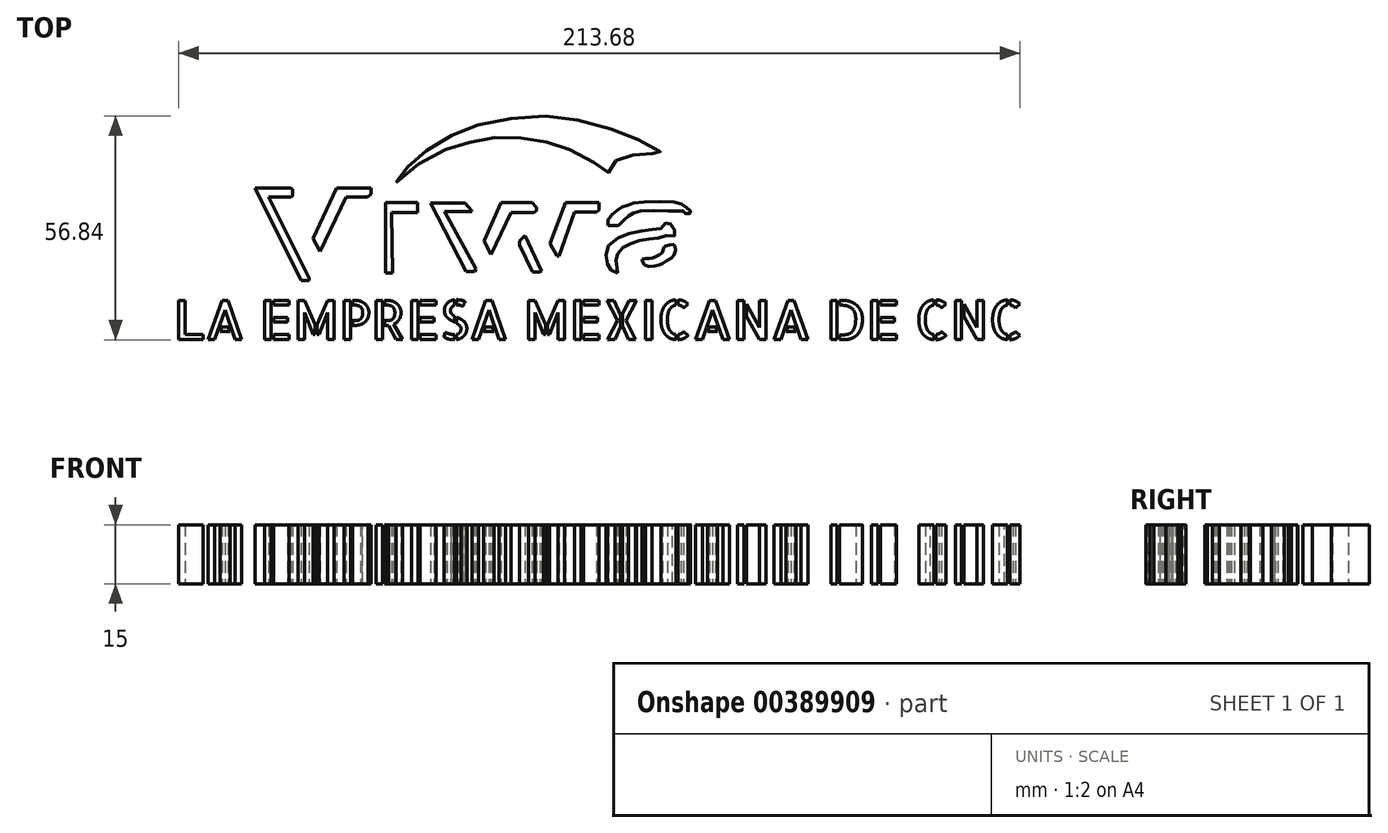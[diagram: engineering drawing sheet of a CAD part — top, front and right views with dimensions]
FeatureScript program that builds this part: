
annotation { "Feature Type Name" : "Feature", "Feature Type Description" : "" }
export const myFeature = defineFeature(function(context is Context, id is Id, definition is map)
    precondition{}
    {
        {
            var Q0;
            Q0=qCreatedBy(makeId("Top.planeOp"),FACE);
            var sketch = newSketch(context, id + "F0", { "sketchPlane" : qUnion([Q0])});
            skLineSegment(sketch, "E0", {"start": v(-40.3, 7.2) * mm, "end": v(-42.29, 7.2) * mm});
            skLineSegment(sketch, "E1", {"start": v(-42.29, 7.2) * mm, "end": v(-54.09, 30.73) * mm});
            skLineSegment(sketch, "E2", {"start": v(-54.09, 30.73) * mm, "end": v(-45.17, 30.73) * mm});
            skLineSegment(sketch, "E3", {"start": v(-45.17, 30.73) * mm, "end": v(-44.48, 30.45) * mm});
            skLineSegment(sketch, "E4", {"start": v(-44.48, 30.45) * mm, "end": v(-44.48, 28.7) * mm});
            skLineSegment(sketch, "E5", {"start": v(-44.48, 28.7) * mm, "end": v(-44.86, 28.36) * mm});
            skLineSegment(sketch, "E6", {"start": v(-44.86, 28.36) * mm, "end": v(-50.58, 28.36) * mm});
            skLineSegment(sketch, "E7", {"start": v(-50.58, 28.36) * mm, "end": v(-40.3, 7.78) * mm});
            skLineSegment(sketch, "E8", {"start": v(-40.3, 7.78) * mm, "end": v(-40.3, 7.2) * mm});
            skLineSegment(sketch, "E9", {"start": v(-37.5, 14.6) * mm, "end": v(-39.26, 17.86) * mm});
            skLineSegment(sketch, "E10", {"start": v(-39.26, 17.86) * mm, "end": v(-33.32, 30.7) * mm});
            skLineSegment(sketch, "E11", {"start": v(-33.32, 30.7) * mm, "end": v(-24.6, 30.7) * mm});
            skLineSegment(sketch, "E12", {"start": v(-24.6, 30.7) * mm, "end": v(-24.6, 29.12) * mm});
            skLineSegment(sketch, "E13", {"start": v(-24.6, 29.12) * mm, "end": v(-25.41, 28.36) * mm});
            skLineSegment(sketch, "E14", {"start": v(-25.41, 28.36) * mm, "end": v(-30.98, 28.36) * mm});
            skLineSegment(sketch, "E15", {"start": v(-30.98, 28.36) * mm, "end": v(-37.5, 14.6) * mm});
            skLineSegment(sketch, "E16", {"start": v(-19.06, 9.07) * mm, "end": v(-20.9, 9.07) * mm});
            skLineSegment(sketch, "E17", {"start": v(-20.9, 9.07) * mm, "end": v(-20.9, 27.04) * mm});
            skLineSegment(sketch, "E18", {"start": v(-20.9, 27.04) * mm, "end": v(-12.74, 27.04) * mm});
            skLineSegment(sketch, "E19", {"start": v(-12.74, 27.04) * mm, "end": v(-12.74, 24.52) * mm});
            skLineSegment(sketch, "E20", {"start": v(-12.74, 24.52) * mm, "end": v(-19.32, 24.52) * mm});
            skLineSegment(sketch, "E21", {"start": v(-19.32, 24.52) * mm, "end": v(-19.06, 9.07) * mm});
            skLineSegment(sketch, "E22", {"start": v(1.67, 9.46) * mm, "end": v(-0.44, 9.46) * mm});
            skLineSegment(sketch, "E23", {"start": v(-0.44, 9.46) * mm, "end": v(-9.5, 26.94) * mm});
            skLineSegment(sketch, "E24", {"start": v(-9.5, 26.94) * mm, "end": v(-0.74, 26.94) * mm});
            skLineSegment(sketch, "E25", {"start": v(-0.74, 26.94) * mm, "end": v(0.92, 25.02) * mm});
            skLineSegment(sketch, "E26", {"start": v(0.92, 25.02) * mm, "end": v(1.08, 24.71) * mm});
            skLineSegment(sketch, "E27", {"start": v(1.08, 24.71) * mm, "end": v(-5.85, 24.71) * mm});
            skLineSegment(sketch, "E28", {"start": v(-5.85, 24.71) * mm, "end": v(2.11, 10.07) * mm});
            skLineSegment(sketch, "E29", {"start": v(2.11, 10.07) * mm, "end": v(1.67, 9.46) * mm});
            skLineSegment(sketch, "E30", {"start": v(4.1, 17.22) * mm, "end": v(8.49, 26.97) * mm});
            skLineSegment(sketch, "E31", {"start": v(8.49, 26.97) * mm, "end": v(16.36, 26.97) * mm});
            skLineSegment(sketch, "E32", {"start": v(16.36, 26.97) * mm, "end": v(17.43, 25.72) * mm});
            skLineSegment(sketch, "E33", {"start": v(17.43, 25.72) * mm, "end": v(17.43, 25) * mm});
            skLineSegment(sketch, "E34", {"start": v(17.43, 25) * mm, "end": v(16.87, 24.52) * mm});
            skLineSegment(sketch, "E35", {"start": v(16.87, 24.52) * mm, "end": v(10.99, 24.52) * mm});
            skLineSegment(sketch, "E36", {"start": v(10.99, 24.52) * mm, "end": v(5.9, 13.87) * mm});
            skLineSegment(sketch, "E37", {"start": v(5.9, 13.87) * mm, "end": v(4.1, 17.22) * mm});
            skLineSegment(sketch, "E38", {"start": v(14.57, 18.65) * mm, "end": v(18.77, 9.66) * mm});
            skLineSegment(sketch, "E39", {"start": v(18.77, 9.66) * mm, "end": v(18.35, 9.3) * mm});
            skLineSegment(sketch, "E40", {"start": v(18.35, 9.3) * mm, "end": v(16.44, 9.3) * mm});
            skLineSegment(sketch, "E41", {"start": v(16.44, 9.3) * mm, "end": v(13.14, 16.2) * mm});
            skLineSegment(sketch, "E42", {"start": v(13.14, 16.2) * mm, "end": v(13.14, 17.22) * mm});
            skLineSegment(sketch, "E43", {"start": v(13.14, 17.22) * mm, "end": v(14.57, 18.65) * mm});
            skLineSegment(sketch, "E44", {"start": v(22.7, 13.37) * mm, "end": v(20.91, 16.54) * mm});
            skLineSegment(sketch, "E45", {"start": v(20.91, 16.54) * mm, "end": v(24.77, 26.96) * mm});
            skLineSegment(sketch, "E46", {"start": v(24.77, 26.96) * mm, "end": v(33.3, 26.96) * mm});
            skLineSegment(sketch, "E47", {"start": v(33.3, 26.96) * mm, "end": v(33.3, 25.07) * mm});
            skLineSegment(sketch, "E48", {"start": v(33.3, 25.07) * mm, "end": v(32.69, 24.54) * mm});
            skLineSegment(sketch, "E49", {"start": v(32.69, 24.54) * mm, "end": v(27.16, 24.54) * mm});
            skLineSegment(sketch, "E50", {"start": v(27.16, 24.54) * mm, "end": v(23.23, 13.45) * mm});
            skLineSegment(sketch, "E51", {"start": v(23.23, 13.45) * mm, "end": v(22.7, 13.37) * mm});
            skLineSegment(sketch, "E52", {"start": v(38.33, 21.2) * mm, "end": v(35.67, 21.2) * mm});
            skFitSpline(sketch, "E53", {"points": [v(35.67, 21.2) * mm, v(35.67, 22.79) * mm, v(37.4, 24.54) * mm, v(38.78, 25.7) * mm, v(41.01, 26.48) * mm, v(42.69, 26.93) * mm, v(52.87, 27.12) * mm, v(54.86, 26.27) * mm, v(56.49, 25.05) * mm, v(56.62, 24.54) * mm, v(56.33, 24.17) * mm, v(55.4, 24.17) * mm, v(54.94, 24.54) * mm, v(54.52, 24.89) * mm, v(53.4, 24.86) * mm, v(44.07, 24.86) * mm, v(41.65, 24.14) * mm, v(40.27, 23.16) * mm, v(38.33, 21.2) * mm], "startDerivative": vector(-7.24, 33.02) * mm, "endDerivative": vector(-30.8, -33.26) * mm});
            skFitSpline(sketch, "E54", {"points": [v(38.01, 9.14) * mm, v(36.65, 9.58) * mm, v(36.21, 10.4) * mm, v(35.39, 11.5) * mm, v(35.1, 13.66) * mm, v(35.67, 15.9) * mm, v(38.33, 18.12) * mm, v(41.87, 19.38) * mm, v(45.5, 20.01) * mm, v(47.75, 20.3) * mm, v(49.52, 20.65) * mm, v(50.15, 21.69) * mm, v(50.7, 21.94) * mm, v(51.39, 21.63) * mm, v(52.37, 20.7) * mm, v(52.59, 19.22) * mm, v(52.56, 18.56) * mm, v(51.17, 18.69) * mm, v(49.62, 18.3) * mm, v(47.85, 17.93) * mm, v(45.38, 17.64) * mm, v(43.2, 17.33) * mm, v(41.3, 16.57) * mm, v(39.53, 15.62) * mm, v(38.33, 14.35) * mm, v(37.73, 13.06) * mm, v(37.63, 12.01) * mm, v(37.82, 10.75) * mm, v(38.33, 9.7) * mm, v(38.01, 9.14) * mm]});
            skFitSpline(sketch, "E55", {"points": [v(44.3, 12.65) * mm, v(45.63, 12.84) * mm, v(46.61, 12.84) * mm, v(47.75, 13.34) * mm, v(48.86, 13.85) * mm, v(49.55, 14.48) * mm, v(49.68, 15.11) * mm, v(49.84, 15.62) * mm, v(50.76, 16.13) * mm, v(52.18, 16.35) * mm, v(52.62, 15.97) * mm, v(52.59, 14) * mm, v(51.58, 12.87) * mm, v(49.3, 11.45) * mm, v(47.88, 10.94) * mm, v(45.29, 10.97) * mm, v(44.43, 11.95) * mm, v(44.3, 12.65) * mm]});
            skFitSpline(sketch, "E56", {"points": [v(-18.25, 32.08) * mm, v(-16.37, 34.86) * mm, v(-11.71, 39.22) * mm, v(-4.34, 43.96) * mm, v(3.86, 47.04) * mm, v(16.56, 48.92) * mm, v(27.92, 48.02) * mm, v(39.42, 44.56) * mm, v(46.34, 41.4) * mm, v(49.5, 39.37) * mm, v(47.55, 39.45) * mm, v(43.18, 39.37) * mm, v(39.72, 38.47) * mm, v(37.02, 37.27) * mm, v(35.67, 35.16) * mm, v(35.67, 34.4) * mm, v(30.7, 38.17) * mm, v(24.16, 41.1) * mm, v(18, 42.9) * mm, v(10.55, 43.58) * mm, v(3.4, 43.13) * mm, v(-3.44, 41.03) * mm, v(-10.13, 38.54) * mm, v(-18.25, 32.08) * mm]});
            skText(sketch, "E57", { "text": "LA EMPRESA MEXICANA DE CNC", "fontName": "AllertaStencil-Regular.ttf"});
            const initialGuessF0  = {"E57": [-0.0747, -0.00779, 1, 0, 0.00996]};
            skSetInitialGuess(sketch, initialGuessF0);
            skSolve(sketch);
        }
        {
            var Q0;
            Q0 = qSketchRegion(id + "F0", true);
            extrude(context, id + "F1", {"entities" : qUnion([Q0]), "depth" : 15 * mm});
        }
    });
